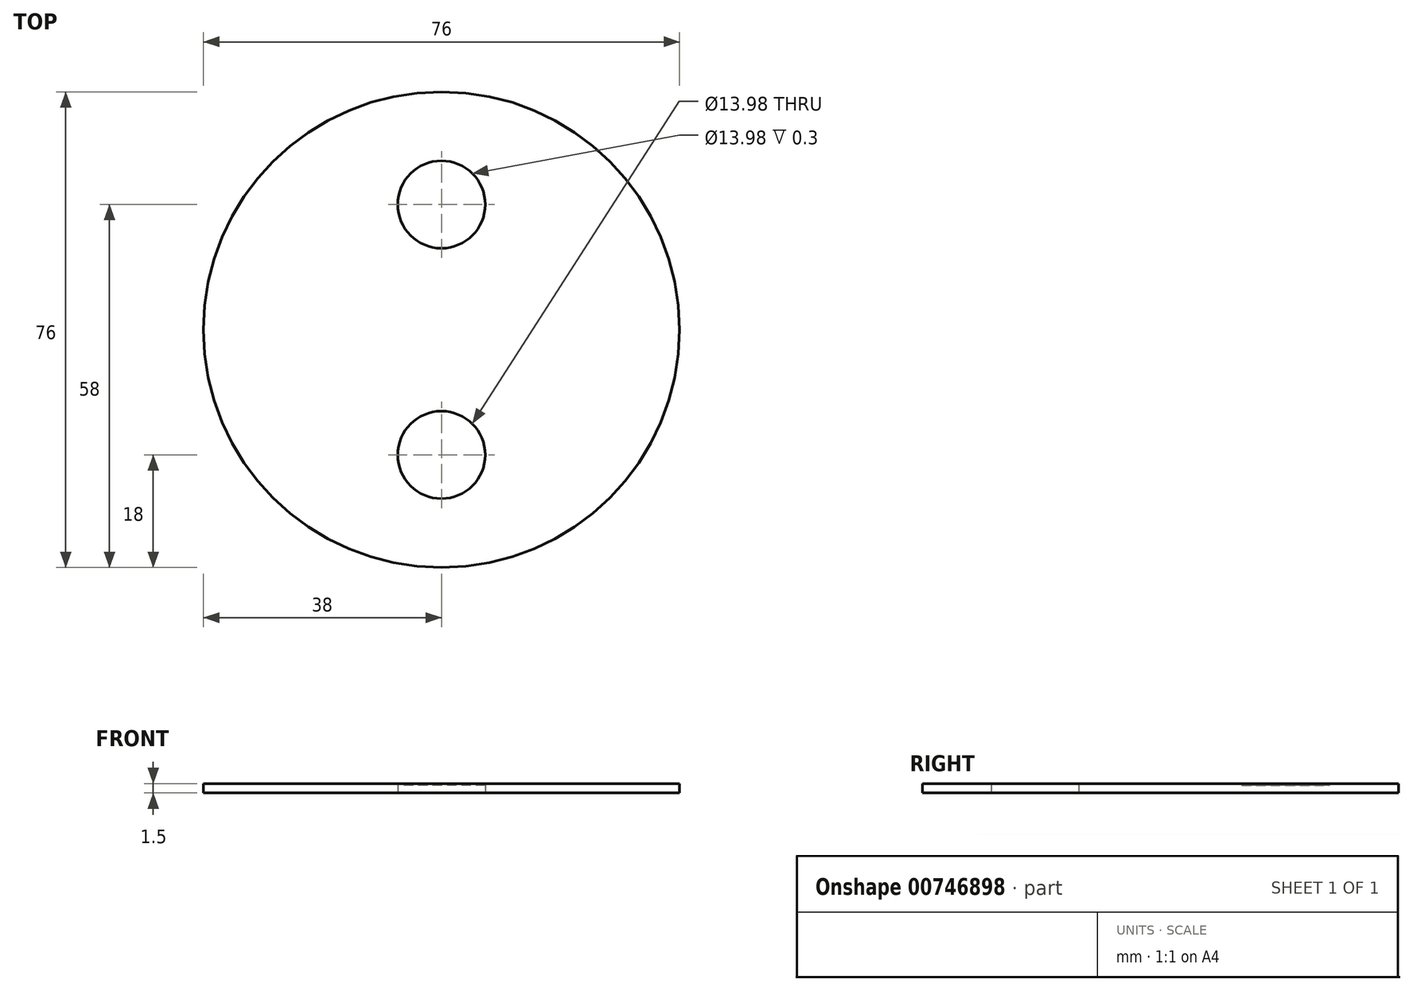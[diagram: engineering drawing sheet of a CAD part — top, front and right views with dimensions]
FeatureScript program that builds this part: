
annotation { "Feature Type Name" : "Feature", "Feature Type Description" : "" }
export const myFeature = defineFeature(function(context is Context, id is Id, definition is map)
    precondition{}
    {
        {
            var Q0;
            Q0=qCreatedBy(makeId("Top.planeOp"),FACE);
            var sketch = newSketch(context, id + "F0", { "sketchPlane" : qUnion([Q0])});
            skCircle(sketch, "E0", {"center": v(0, 0) * mm, "radius": 38 * mm});
            skLineSegment(sketch, "E1", {"start": v(-40.6, 0) * mm, "end": v(41.06, 0) * mm, "construction": true});
            skLineSegment(sketch, "E2", {"start": v(0, 40.01) * mm, "end": v(0, -40.33) * mm, "construction": true});
            skCircle(sketch, "E3", {"center": v(0, 20) * mm, "radius": 7 * mm});
            skCircle(sketch, "E4.MirrorC", {"center": v(0, -20) * mm, "radius": 7 * mm});
            skSolve(sketch);
        }
        {
            var Q0;
            Q0=makeQuery(id+"F0.imprint","IMPRINT",FACE,{"disambiguationData":[TD([[makeQuery(id+"F0.imprint","IMPRINT",EDGE,{"derivedFrom":sQuery(id+"F0.wireOp",EDGE,"E3")}),1.0]])]});
            var Q1;
            Q1=makeQuery(id+"F0.imprint","IMPRINT",FACE,{"disambiguationData":[TD([[makeQuery(id+"F0.imprint","IMPRINT",EDGE,{"derivedFrom":sQuery(id+"F0.wireOp",EDGE,"E4.MirrorC")}),-1.0]])]});
            extrude(context, id + "F1", {"entities" : qUnion([Q0, Q1]), "depth" : 1.2 * mm, "offsetDistance" : 25 * mm});
        }
        {
            var Q0;
            Q0 = qSketchRegion(id + "F0", true);
            extrude(context, id + "F2", {"entities" : qUnion([Q0]), "operationType" : NewBodyOperationType.ADD, "depth" : 1.5 * mm, "offsetDistance" : 25 * mm});
        }
    });
